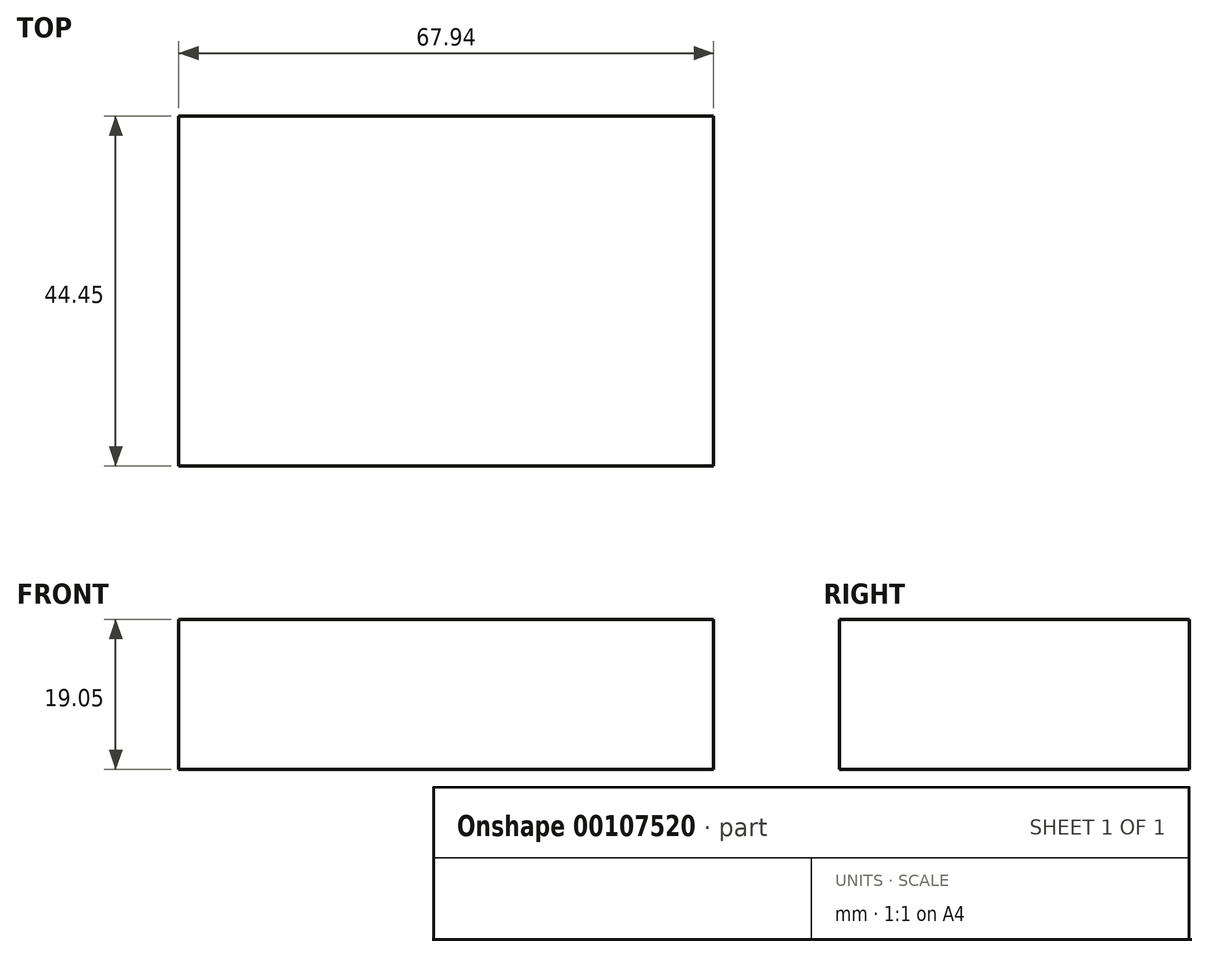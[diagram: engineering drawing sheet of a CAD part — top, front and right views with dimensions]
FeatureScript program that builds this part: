
annotation { "Feature Type Name" : "Feature", "Feature Type Description" : "" }
export const myFeature = defineFeature(function(context is Context, id is Id, definition is map)
    precondition{}
    {
        {
            var Q0;
            Q0=qCreatedBy(makeId("Front.planeOp"),FACE);
            var sketch = newSketch(context, id + "F0", { "sketchPlane" : qUnion([Q0])});
            skLineSegment(sketch, "E0.bottom", {"start": v(-31.31, -12.4) * mm, "end": v(36.63, -12.4) * mm});
            skLineSegment(sketch, "E0.top", {"start": v(-31.31, 6.64) * mm, "end": v(36.63, 6.64) * mm});
            skLineSegment(sketch, "E0.left", {"start": v(-31.31, -12.4) * mm, "end": v(-31.31, 6.64) * mm});
            skLineSegment(sketch, "E0.right", {"start": v(36.63, -12.4) * mm, "end": v(36.63, 6.64) * mm});
            skSolve(sketch);
        }
        {
            var Q0;
            Q0 = qSketchRegion(id + "F0", true);
            extrude(context, id + "F1", {"entities" : qUnion([Q0]), "depth" : 44.45 * mm});
        }
    });
